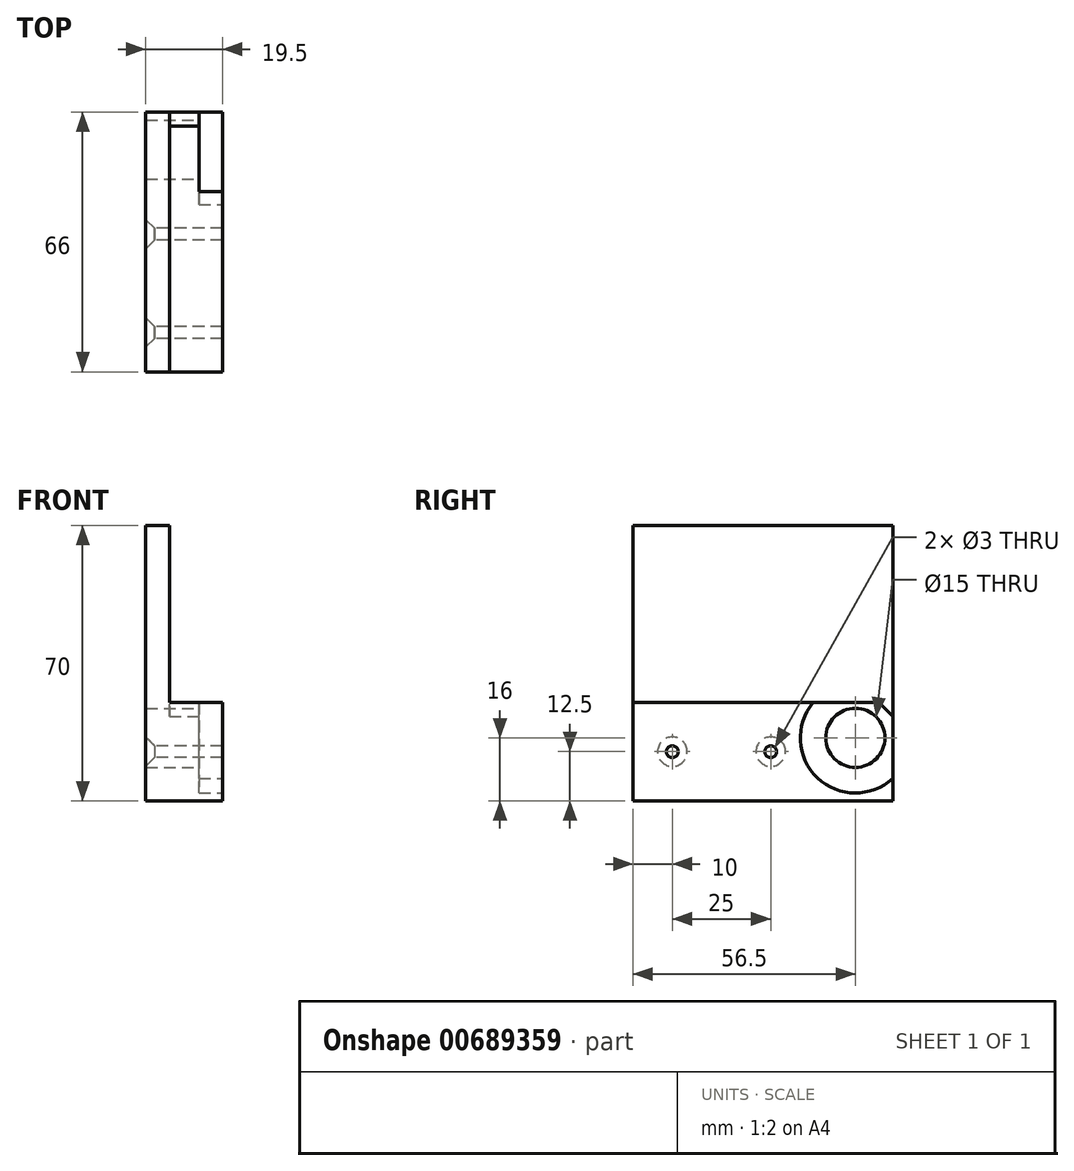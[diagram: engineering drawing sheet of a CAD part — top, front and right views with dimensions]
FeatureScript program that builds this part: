
annotation { "Feature Type Name" : "Feature", "Feature Type Description" : "" }
export const myFeature = defineFeature(function(context is Context, id is Id, definition is map)
    precondition{}
    {
        {
            var Q0;
            Q0=qCreatedBy(makeId("Front.planeOp"),FACE);
            var sketch = newSketch(context, id + "F0", { "sketchPlane" : qUnion([Q0])});
            skLineSegment(sketch, "E0", {"start": v(0, 0) * mm, "end": v(0, 70) * mm});
            skLineSegment(sketch, "E1", {"start": v(0, 0) * mm, "end": v(19.5, 0) * mm});
            skLineSegment(sketch, "E2", {"start": v(19.5, 25) * mm, "end": v(6, 25) * mm});
            skLineSegment(sketch, "E3", {"start": v(6, 70) * mm, "end": v(6, 25) * mm});
            skLineSegment(sketch, "E4", {"start": v(0, 70) * mm, "end": v(6, 70) * mm});
            skLineSegment(sketch, "E5", {"start": v(19.5, 0) * mm, "end": v(19.5, 25) * mm});
            skSolve(sketch);
        }
        {
            var Q0;
            Q0=qSketchRegion(id+"F0",true);
            extrude(context, id + "F1", {"entities" : qUnion([Q0]), "depth" : 66 * mm});
        }
        {
            var Q0;
            Q0=makeQuery(id+"F1.opExtrude","SWEPT_FACE",FACE,{"disambiguationData":[OSD([sQuery(id+"F0.wireOp",EDGE,"E5")])]});
            var sketch = newSketch(context, id + "F2", { "sketchPlane" : qUnion([Q0])});
            skLineSegment(sketch, "E6", {"start": v(-33, 36.84) * mm, "end": v(-33, -7.5) * mm, "construction": true});
            skLineSegment(sketch, "E7", {"start": v(9.43, 28) * mm, "end": v(-80.2, 28) * mm, "construction": true});
            skLineSegment(sketch, "E8", {"start": v(9.43, 16) * mm, "end": v(-79.93, 16) * mm, "construction": true});
            skLineSegment(sketch, "E9", {"start": v(-71, 47.6) * mm, "end": v(-71, -9.4) * mm, "construction": true});
            skLineSegment(sketch, "E10", {"start": v(-56.5, 16.24) * mm, "end": v(-56.5, 4.24) * mm, "construction": true});
            skLineSegment(sketch, "E11", {"start": v(5, 48.77) * mm, "end": v(5, -8.97) * mm, "construction": true});
            skLineSegment(sketch, "E12", {"start": v(-9.5, 16.43) * mm, "end": v(-9.5, 4.8) * mm, "construction": true});
            skCircle(sketch, "E13", {"center": v(-9.5, 16) * mm, "radius": 7.5 * mm});
            skSolve(sketch);
        }
        {
            var Q0;
            Q0=qSketchRegion(id+"F2",true);
            extrude(context, id + "F3", {"entities" : qUnion([Q0]), "operationType" : NewBodyOperationType.REMOVE, "endBound" : BoundingType.THROUGH_ALL, "oppositeDirection" : true, "depth" : 25 * mm});
        }
        {
            var Q0;
            Q0=makeQuery(id+"F1.opExtrude","SWEPT_FACE",FACE,{"disambiguationData":[OSD([sQuery(id+"F0.wireOp",EDGE,"E5")])]});
            var sketch = newSketch(context, id + "F4", { "sketchPlane" : qUnion([Q0])});
            skPoint(sketch, "E14.orphan", {"position": v(-9.5, 16) * mm});
            skPoint(sketch, "E15.orphan", {"position": v(-44.75, 0) * mm});
            skPoint(sketch, "E16.orphan", {"position": v(-43.5, 0) * mm});
            skLineSegment(sketch, "E17.trimOffspring", {"start": v(-20.22, 25) * mm, "end": v(0, 25) * mm});
            skLineSegment(sketch, "E18", {"start": v(0, 25) * mm, "end": v(0, 0) * mm});
            skArc(sketch, "E19.converted", {"start": v(-20.22, 25) * mm, "mid": v(-19.16, 5.87) * mm, "end": v(0, 5.72) * mm});
            skSolve(sketch);
        }
        {
            var Q0;
            Q0=qSketchRegion(id+"F4",true);
            extrude(context, id + "F5", {"entities" : qUnion([Q0]), "operationType" : NewBodyOperationType.REMOVE, "oppositeDirection" : true, "depth" : 6 * mm});
        }
        {
            var Q0;
            Q0=makeQuery(id+"F1.opExtrude","SWEPT_FACE",FACE,{"disambiguationData":[OSD([sQuery(id+"F0.wireOp",EDGE,"E5")])]});
            var sketch = newSketch(context, id + "F6", { "sketchPlane" : qUnion([Q0])});
            skLineSegment(sketch, "E20", {"start": v(0, 21.5) * mm, "end": v(0, 25) * mm});
            skLineSegment(sketch, "E21", {"start": v(-3.5, 25) * mm, "end": v(0, 25) * mm});
            skLineSegment(sketch, "E22", {"start": v(0, 21.5) * mm, "end": v(-3.5, 25) * mm});
            skSolve(sketch);
        }
        {
            var Q0;
            Q0=qSketchRegion(id+"F6",true);
            extrude(context, id + "F7", {"entities" : qUnion([Q0]), "operationType" : NewBodyOperationType.REMOVE, "oppositeDirection" : true, "depth" : 13.5 * mm});
        }
        {
            var Q0;
            Q0=makeQuery(id+"F7.boolean.opBoolean","MERGE",FACE,{"derivedFrom":[makeQuery(id+"F1.opExtrude","SWEPT_FACE",FACE,{"disambiguationData":[OSD([sQuery(id+"F0.wireOp",EDGE,"E3")])]}),makeQuery(id+"F7.opExtrude","CAP_FACE",FACE,{"disambiguationData":[OSD([sQuery(id+"F6.wireOp",EDGE,"E20"),sQuery(id+"F6.wireOp",EDGE,"E21"),sQuery(id+"F6.wireOp",EDGE,"E22")])],"isStart":false})]});
            var sketch = newSketch(context, id + "F8", { "sketchPlane" : qUnion([Q0])});
            skCircle(sketch, "E23", {"center": v(-17.5, 82.5) * mm, "radius": 1.5 * mm});
            skCircle(sketch, "E24", {"center": v(-48.5, 82.5) * mm, "radius": 1.5 * mm});
            skSolve(sketch);
        }
        {
            var Q0;
            Q0=qSketchRegion(id+"F8",true);
            extrude(context, id + "F9", {"entities" : qUnion([Q0]), "operationType" : NewBodyOperationType.REMOVE, "endBound" : BoundingType.THROUGH_ALL, "oppositeDirection" : true, "depth" : 25 * mm, "offsetDistance" : 25 * mm});
        }
        {
            var Q0;
            Q0=makeQuery(id+"F1.opExtrude","SWEPT_FACE",FACE,{"disambiguationData":[OSD([sQuery(id+"F0.wireOp",EDGE,"E0")])]});
            var sketch = newSketch(context, id + "F10", { "sketchPlane" : qUnion([Q0])});
            skPoint(sketch, "E25", {"position": v(56, 12.5) * mm});
            skPoint(sketch, "E26", {"position": v(31, 12.5) * mm});
            skSolve(sketch);
        }
        {
            var Q0;
            Q0=sQuery(id+"F10.wireOp",VERTEX,"E26");
            var Q1;
            Q1=sQuery(id+"F10.wireOp",VERTEX,"E25");
            var Q2;
            Q2=sQuery(id+"F10.wireOp",VERTEX,"E25");
            var Q3;
            Q3=makeQuery(id+"F1.opExtrude","SWEPT_BODY",BODY,{"disambiguationData":[OSD([sQuery(id+"F0.wireOp",EDGE,"E0"),sQuery(id+"F0.wireOp",EDGE,"E1"),sQuery(id+"F0.wireOp",EDGE,"E2"),sQuery(id+"F0.wireOp",EDGE,"E3"),sQuery(id+"F0.wireOp",EDGE,"E4"),sQuery(id+"F0.wireOp",EDGE,"E5")])]});
            hole(context, id + "F11", {"style" : HoleStyle.C_SINK, "endStyle" : HoleEndStyle.THROUGH, "holeDiameter" : 3 * mm, "cSinkDiameter" : 7.5 * mm, "cSinkAngle" : 90 * degree, "majorDiameter" : 5 * mm, "isTappedThrough" : true, "tappedDepth" : 12 * mm, "tapClearance" : 3, "startFromSketch" : true, "locations" : qUnion([Q0, Q1, Q2]), "scope" : qUnion([Q3])});
        }
    });
